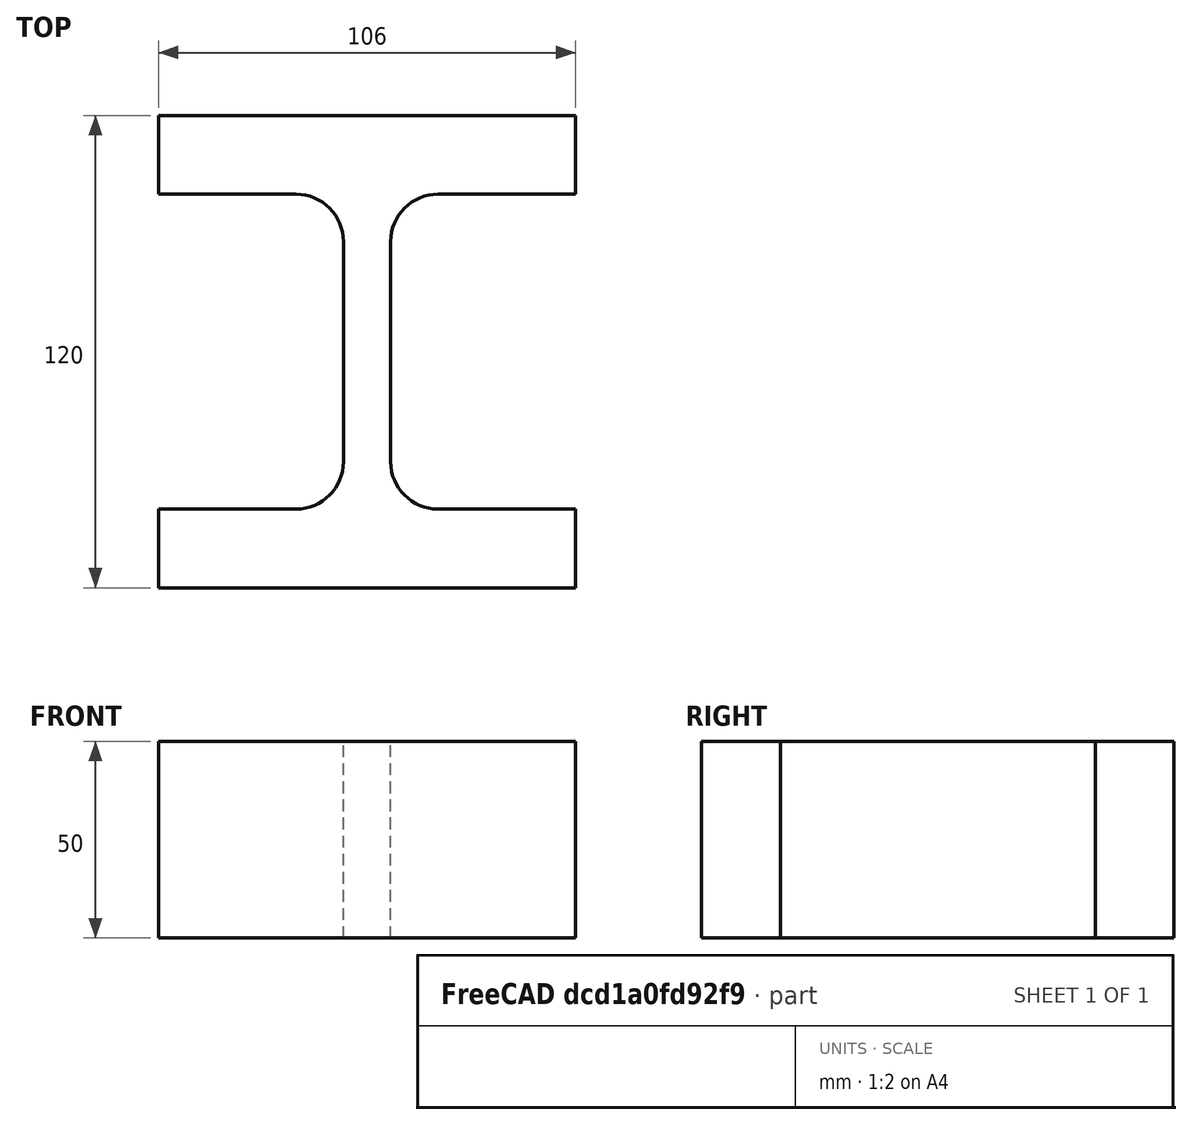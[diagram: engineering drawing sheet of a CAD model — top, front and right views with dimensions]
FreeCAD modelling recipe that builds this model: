
FCSTD DOCUMENT  (FreeCAD 0.15R4671 (Git))
Label: HE-M-Profile 100 DIN1025-4 S235JR
License: All rights reserved
LicenseURL: http://en.wikipedia.org/wiki/All_rights_reserved
objects: Sketcher::SketchObject×1, Part::Extrusion×1
note: 2 computed .brp shape members not serialized (recipe doc carries the construction recipe); baked Part::Feature solids carry a one-line shape summary decoded from their .brp

FEATURE [Sketcher::SketchObject] Sketch
  sketch-geometry (16):
    g0: LineSegment StartX=6 StartY=-28 StartZ=0 EndX=6 EndY=28 EndZ=0
    g1: LineSegment StartX=18 StartY=40 StartZ=0 EndX=53 EndY=40 EndZ=0
    g2: LineSegment StartX=53 StartY=40 StartZ=0 EndX=53 EndY=60 EndZ=0
    g3: LineSegment StartX=53 StartY=60 StartZ=0 EndX=-53 EndY=60 EndZ=0
    g4: LineSegment StartX=-53 StartY=60 StartZ=0 EndX=-53 EndY=40 EndZ=0
    g5: LineSegment StartX=-53 StartY=40 StartZ=0 EndX=-18 EndY=40 EndZ=0
    g6: LineSegment StartX=-6 StartY=28 StartZ=0 EndX=-6 EndY=-28 EndZ=0
    g7: LineSegment StartX=-18 StartY=-40 StartZ=0 EndX=-53 EndY=-40 EndZ=0
    g8: LineSegment StartX=-53 StartY=-40 StartZ=0 EndX=-53 EndY=-60 EndZ=0
    g9: LineSegment StartX=-53 StartY=-60 StartZ=0 EndX=53 EndY=-60 EndZ=0
    g10: LineSegment StartX=53 StartY=-60 StartZ=0 EndX=53 EndY=-40 EndZ=0
    g11: LineSegment StartX=53 StartY=-40 StartZ=0 EndX=18 EndY=-40 EndZ=0
    g12: ArcOfCircle CenterX=18 CenterY=28 CenterZ=0 NormalX=0 NormalY=0 NormalZ=1 Radius=12 StartAngle=1.5708 EndAngle=3.14159
    g13: ArcOfCircle CenterX=18 CenterY=-28 CenterZ=0 NormalX=0 NormalY=0 NormalZ=1 Radius=12 StartAngle=3.14159 EndAngle=4.71239
    g14: ArcOfCircle CenterX=-18 CenterY=28 CenterZ=0 NormalX=0 NormalY=0 NormalZ=1 Radius=12 StartAngle=0 EndAngle=1.5708
    g15: ArcOfCircle CenterX=-18 CenterY=-28 CenterZ=0 NormalX=0 NormalY=0 NormalZ=1 Radius=12 StartAngle=4.71239 EndAngle=6.28319
  constraints (42):
    c: Vertical(g0)
    c: Coincident(g2,g1)
    c: Vertical(g2)
    c: Coincident(g3,g2)
    c: Coincident(g4,g3)
    c: Vertical(g4)
    c: Coincident(g5,g4)
    c: Horizontal(g5)
    c: Vertical(g6)
    c: Horizontal(g7)
    c: Coincident(g8,g7)
    c: Vertical(g8)
    c: Coincident(g9,g8)
    c: Horizontal(g9)
    c: Coincident(g10,g9)
    c: Vertical(g10)
    c: Coincident(g11,g10)
    c: Horizontal(g11)
    c: Tangent(g1,g12) = 1.5708
    c: Tangent(g0,g12) = 1.5708
    c: Tangent(g0,g13) = 1.5708
    c: Tangent(g11,g13) = 1.5708
    c: Tangent(g5,g14) = 1.5708
    c: Tangent(g6,g14) = 1.5708
    c: Tangent(g6,g15) = 1.5708
    c: Tangent(g7,g15) = 1.5708
    c: Equal(g3,g9)
    c: Equal(g2,g4)
    c: Equal(g4,g8)
    c: Equal(g8,g10)
    c: Equal(g12,g14)
    c: Equal(g14,g15)
    c: Equal(g15,g13)
    c: Symmetric(g2,g3,g-2)
    c: Symmetric(g9,g8,g-2)
    c: Symmetric(g0,g6,g-2)
    c: Symmetric(g2,g9,g-1)
    c: DistanceY(g2,g9) = -120
    c: DistanceX(g3) = -106
    c: DistanceX(g0,g6) = -12
    c: DistanceY(g2) = 20
    c: Radius(g12) = 12
FEATURE [Part::Extrusion] Extrude  label="HE-M-Profile 100 DIN1025-4 S235JR"
  Base = -> Sketch
  Dir = (0,0,50)
  Solid = true
